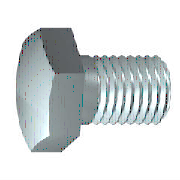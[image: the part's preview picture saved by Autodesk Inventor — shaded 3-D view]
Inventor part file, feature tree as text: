
AUTODESK INVENTOR PART (.ipt)
format: ipt  version: 2023.2 (Build 272271030, 271C)  size: 200,192 bytes
history: native  units: mm (DEFAULTED — no unit token found)
features: sketch x4, other x4, plane x3, chamfer x1, fillet x1
ambient origin geometry x6: Origin, XY Plane, X Axis, Y Axis, Z Axis, Center Point
bodies: Solid1 (feature_tree)
feature tree (13):
  plane  "WorkPlane1"
  sketch  "Sketch1"  dims[d0=30.0mm]
  other  "WorkPoint1"
  chamfer  "Chamfer1"  Distance=4.0mm
  fillet  "Fillet1"  [1 undecoded]
  other  "MSC_A1"
  other  "MSC_PF1"
  other  "MSC_PT1"
  plane  "WorkPlane2"
  plane  "WorkPlane3"
  sketch  "Sketch2"  dims[d1=10.0mm]
  sketch  "Sketch3"  dims[d2=15.0mm]
  sketch  "Sketch4"  dims[d4=17.321016mm d6=4.0mm d7=0.0mm d8=15.0mm d10=0.0mm d12=30.0deg d14=360.0deg d15=0.0mm d17=10.0mm d18=3.0mm d19=80.0mm d20=30.0mm d21=360.0deg d22=0.5mm d23=0.5mm d24=0.25mm d25=0.1mm d26=0.0mm d27=60.0deg d28=5.0mm d29=0.0mm d30=0.0mm d32=0.0mm d33=0.0mm d34=0.0mm d37=0.0mm d38=0.0mm d39=45.0deg d40=0.0mm d41=0.0mm d42=0.0mm]
note: 1 required parameter value undecoded (feature->parameter linkage not recoverable at this tier; creation-order binding heuristic only, values carry confidence <= 0.55)
